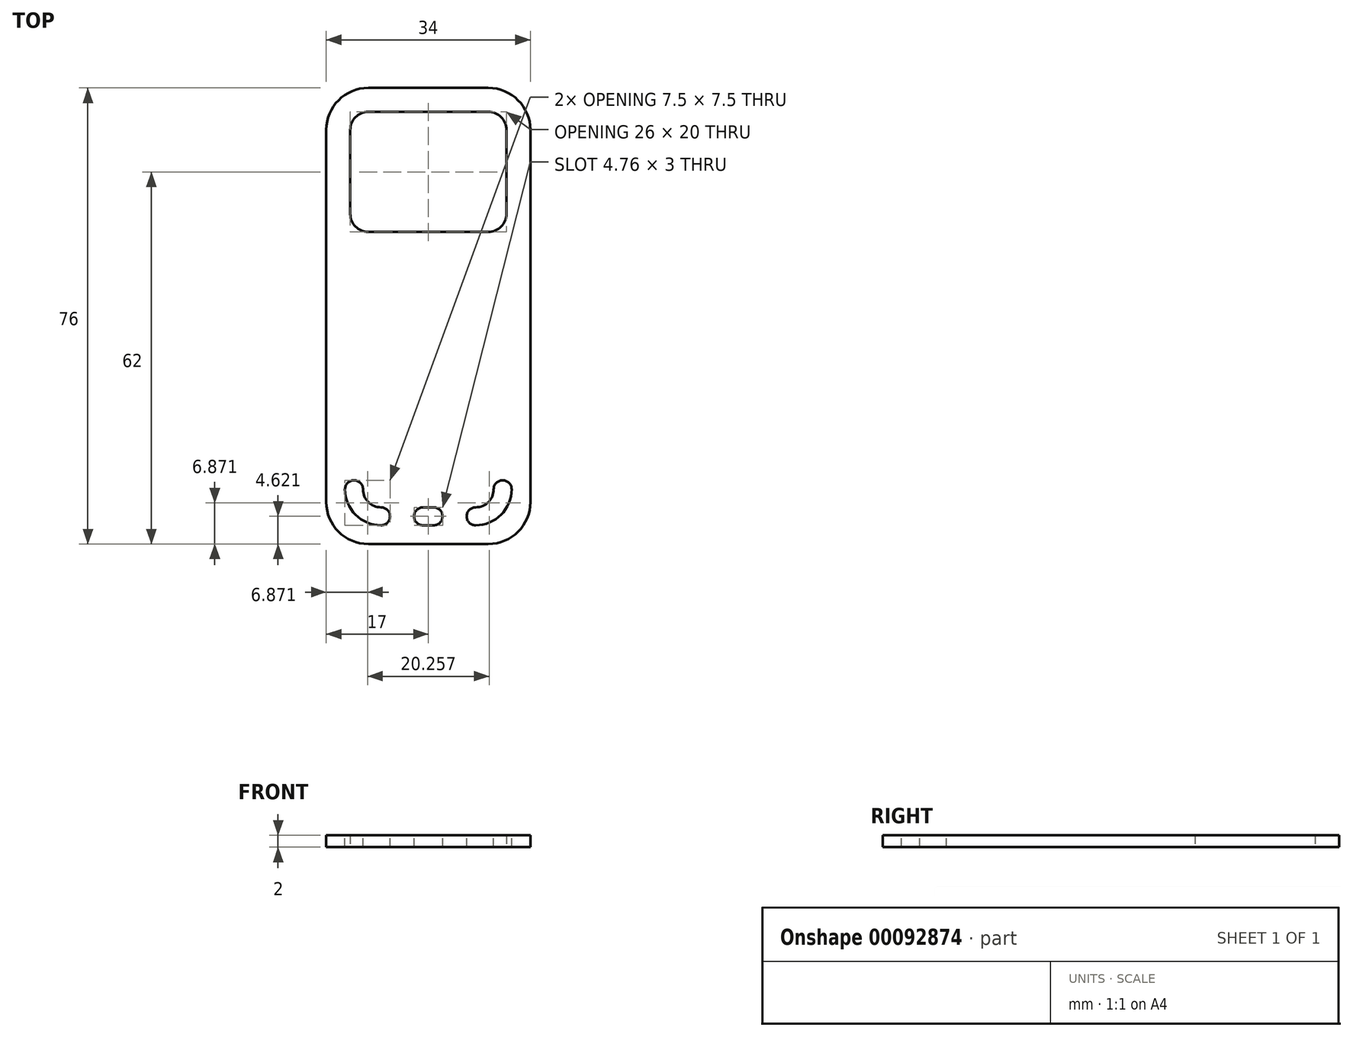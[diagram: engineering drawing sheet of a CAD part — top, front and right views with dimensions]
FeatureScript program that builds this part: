
annotation { "Feature Type Name" : "Feature", "Feature Type Description" : "" }
export const myFeature = defineFeature(function(context is Context, id is Id, definition is map)
    precondition{}
    {
        {
            var Q0;
            Q0=qCreatedBy(makeId("Top.planeOp"),FACE);
            var sketch = newSketch(context, id + "F0", { "sketchPlane" : qUnion([Q0])});
            skLineSegment(sketch, "E0.bottom", {"start": v(0, 0) * mm, "end": v(34, 0) * mm});
            skLineSegment(sketch, "E0.top", {"start": v(0, 76) * mm, "end": v(34, 76) * mm});
            skLineSegment(sketch, "E0.left", {"start": v(0, 0) * mm, "end": v(0, 76) * mm});
            skLineSegment(sketch, "E0.right", {"start": v(34, 0) * mm, "end": v(34, 76) * mm});
            skLineSegment(sketch, "E1.bottom", {"start": v(4, 72) * mm, "end": v(30, 72) * mm});
            skLineSegment(sketch, "E1.top", {"start": v(4, 52) * mm, "end": v(30, 52) * mm});
            skLineSegment(sketch, "E1.left", {"start": v(4, 72) * mm, "end": v(4, 52) * mm});
            skLineSegment(sketch, "E1.right", {"start": v(30, 72) * mm, "end": v(30, 52) * mm});
            skSolve(sketch);
        }
        {
            var Q0;
            Q0=makeQuery(id+"F0.imprint","IMPRINT",FACE,{"disambiguationData":[TD([[makeQuery(id+"F0.imprint","IMPRINT",EDGE,{"derivedFrom":sQuery(id+"F0.wireOp",EDGE,"E0.bottom")}),1.0]])]});
            extrude(context, id + "F1", {"entities" : qUnion([Q0]), "depth" : 2 * mm});
        }
        {
            var Q0;
            Q0=makeQuery(id+"F1.opExtrude","SWEPT_EDGE",EDGE,{"disambiguationData":[OSD([sQuery(id+"F0.wireOp",EDGE,"E1.bottom"),sQuery(id+"F0.wireOp",EDGE,"E1.left")])]});
            var Q1;
            Q1=makeQuery(id+"F1.opExtrude","SWEPT_EDGE",EDGE,{"disambiguationData":[OSD([sQuery(id+"F0.wireOp",EDGE,"E1.bottom"),sQuery(id+"F0.wireOp",EDGE,"E1.right")])]});
            var Q2;
            Q2=makeQuery(id+"F1.opExtrude","SWEPT_EDGE",EDGE,{"disambiguationData":[OSD([sQuery(id+"F0.wireOp",EDGE,"E1.top"),sQuery(id+"F0.wireOp",EDGE,"E1.right")])]});
            var Q3;
            Q3=makeQuery(id+"F1.opExtrude","SWEPT_EDGE",EDGE,{"disambiguationData":[OSD([sQuery(id+"F0.wireOp",EDGE,"E1.top"),sQuery(id+"F0.wireOp",EDGE,"E1.left")])]});
            fillet(context, id + "F2", {"entities" : qUnion([Q0, Q1, Q2, Q3]), "radius" : 3 * mm, "tangentPropagation" : true, "allowEdgeOverflow" : false});
        }
        {
            var Q0;
            Q0=makeQuery(id+"F1.opExtrude","SWEPT_EDGE",EDGE,{"disambiguationData":[OSD([sQuery(id+"F0.wireOp",EDGE,"E0.top"),sQuery(id+"F0.wireOp",EDGE,"E0.right")])]});
            var Q1;
            Q1=makeQuery(id+"F1.opExtrude","SWEPT_EDGE",EDGE,{"disambiguationData":[OSD([sQuery(id+"F0.wireOp",EDGE,"E0.top"),sQuery(id+"F0.wireOp",EDGE,"E0.left")])]});
            var Q2;
            Q2=makeQuery(id+"F1.opExtrude","SWEPT_EDGE",EDGE,{"disambiguationData":[OSD([sQuery(id+"F0.wireOp",EDGE,"E0.bottom"),sQuery(id+"F0.wireOp",EDGE,"E0.left")])]});
            var Q3;
            Q3=makeQuery(id+"F1.opExtrude","SWEPT_EDGE",EDGE,{"disambiguationData":[OSD([sQuery(id+"F0.wireOp",EDGE,"E0.bottom"),sQuery(id+"F0.wireOp",EDGE,"E0.right")])]});
            fillet(context, id + "F3", {"entities" : qUnion([Q0, Q1, Q2, Q3]), "radius" : 7 * mm, "tangentPropagation" : true, "allowEdgeOverflow" : false});
        }
        {
            var Q0;
            Q0=makeQuery(id+"F1.opExtrude","CAP_FACE",FACE,{"disambiguationData":[OSD([sQuery(id+"F0.wireOp",EDGE,"E0.bottom"),sQuery(id+"F0.wireOp",EDGE,"E0.top"),sQuery(id+"F0.wireOp",EDGE,"E0.left"),sQuery(id+"F0.wireOp",EDGE,"E0.right"),sQuery(id+"F0.wireOp",EDGE,"E1.bottom"),sQuery(id+"F0.wireOp",EDGE,"E1.top"),sQuery(id+"F0.wireOp",EDGE,"E1.left"),sQuery(id+"F0.wireOp",EDGE,"E1.right")])],"isStart":false});
            var sketch = newSketch(context, id + "F4", { "sketchPlane" : qUnion([Q0])});
            skCircle(sketch, "E2", {"center": v(7, 7) * mm, "radius": 3 * mm, "construction": true});
            skCircle(sketch, "E3", {"center": v(27, 7) * mm, "radius": 3 * mm, "construction": true});
            skCircle(sketch, "E4", {"center": v(9.12, 9.12) * mm, "radius": 3 * mm, "construction": true});
            skCircle(sketch, "E5", {"center": v(9.12, 9.12) * mm, "radius": 6 * mm, "construction": true});
            skCircle(sketch, "E6", {"center": v(24.88, 9.12) * mm, "radius": 3 * mm, "construction": true});
            skCircle(sketch, "E7", {"center": v(24.88, 9.12) * mm, "radius": 6 * mm, "construction": true});
            skCircle(sketch, "E8", {"center": v(16.12, 4.62) * mm, "radius": 1.5 * mm, "construction": true});
            skCircle(sketch, "E9", {"center": v(17.88, 4.62) * mm, "radius": 1.5 * mm, "construction": true});
            skArc(sketch, "E10", {"start": v(3.12, 9.12) * mm, "mid": v(4.88, 4.88) * mm, "end": v(9.12, 3.12) * mm});
            skArc(sketch, "E11", {"start": v(6.12, 9.12) * mm, "mid": v(7, 7) * mm, "end": v(9.12, 6.12) * mm});
            skArc(sketch, "E12", {"start": v(9.12, 3.12) * mm, "mid": v(10.62, 4.62) * mm, "end": v(9.12, 6.12) * mm});
            skArc(sketch, "E13", {"start": v(6.12, 9.12) * mm, "mid": v(4.62, 10.62) * mm, "end": v(3.12, 9.12) * mm});
            skArc(sketch, "E14", {"start": v(24.88, 6.12) * mm, "mid": v(27, 7) * mm, "end": v(27.88, 9.12) * mm});
            skArc(sketch, "E15", {"start": v(24.88, 3.12) * mm, "mid": v(29.12, 4.88) * mm, "end": v(30.88, 9.12) * mm});
            skArc(sketch, "E16", {"start": v(24.88, 6.12) * mm, "mid": v(23.38, 4.62) * mm, "end": v(24.88, 3.12) * mm});
            skArc(sketch, "E17", {"start": v(30.88, 9.12) * mm, "mid": v(29.38, 10.62) * mm, "end": v(27.88, 9.12) * mm});
            skLineSegment(sketch, "E18", {"start": v(16.12, 6.12) * mm, "end": v(17.88, 6.12) * mm});
            skLineSegment(sketch, "E19", {"start": v(16.12, 3.12) * mm, "end": v(17.88, 3.12) * mm});
            skArc(sketch, "E20", {"start": v(16.12, 6.12) * mm, "mid": v(14.62, 4.62) * mm, "end": v(16.12, 3.12) * mm});
            skArc(sketch, "E21", {"start": v(17.88, 3.12) * mm, "mid": v(19.38, 4.62) * mm, "end": v(17.88, 6.12) * mm});
            skSolve(sketch);
        }
        {
            var Q0;
            Q0=makeQuery(id+"F4.imprint","IMPRINT",FACE,{"disambiguationData":[TD([[makeQuery(id+"F4.imprint","IMPRINT",EDGE,{"derivedFrom":sQuery(id+"F4.wireOp",EDGE,"E10")}),1.0]])]});
            var Q1;
            Q1=makeQuery(id+"F4.imprint","IMPRINT",FACE,{"disambiguationData":[TD([[makeQuery(id+"F4.imprint","IMPRINT",EDGE,{"derivedFrom":sQuery(id+"F4.wireOp",EDGE,"E18")}),-1.0]])]});
            var Q2;
            Q2=makeQuery(id+"F4.imprint","IMPRINT",FACE,{"disambiguationData":[TD([[makeQuery(id+"F4.imprint","IMPRINT",EDGE,{"derivedFrom":sQuery(id+"F4.wireOp",EDGE,"E14")}),-1.0]])]});
            extrude(context, id + "F5", {"entities" : qUnion([Q0, Q1, Q2]), "operationType" : NewBodyOperationType.REMOVE, "oppositeDirection" : true, "depth" : 25 * mm});
        }
    });
